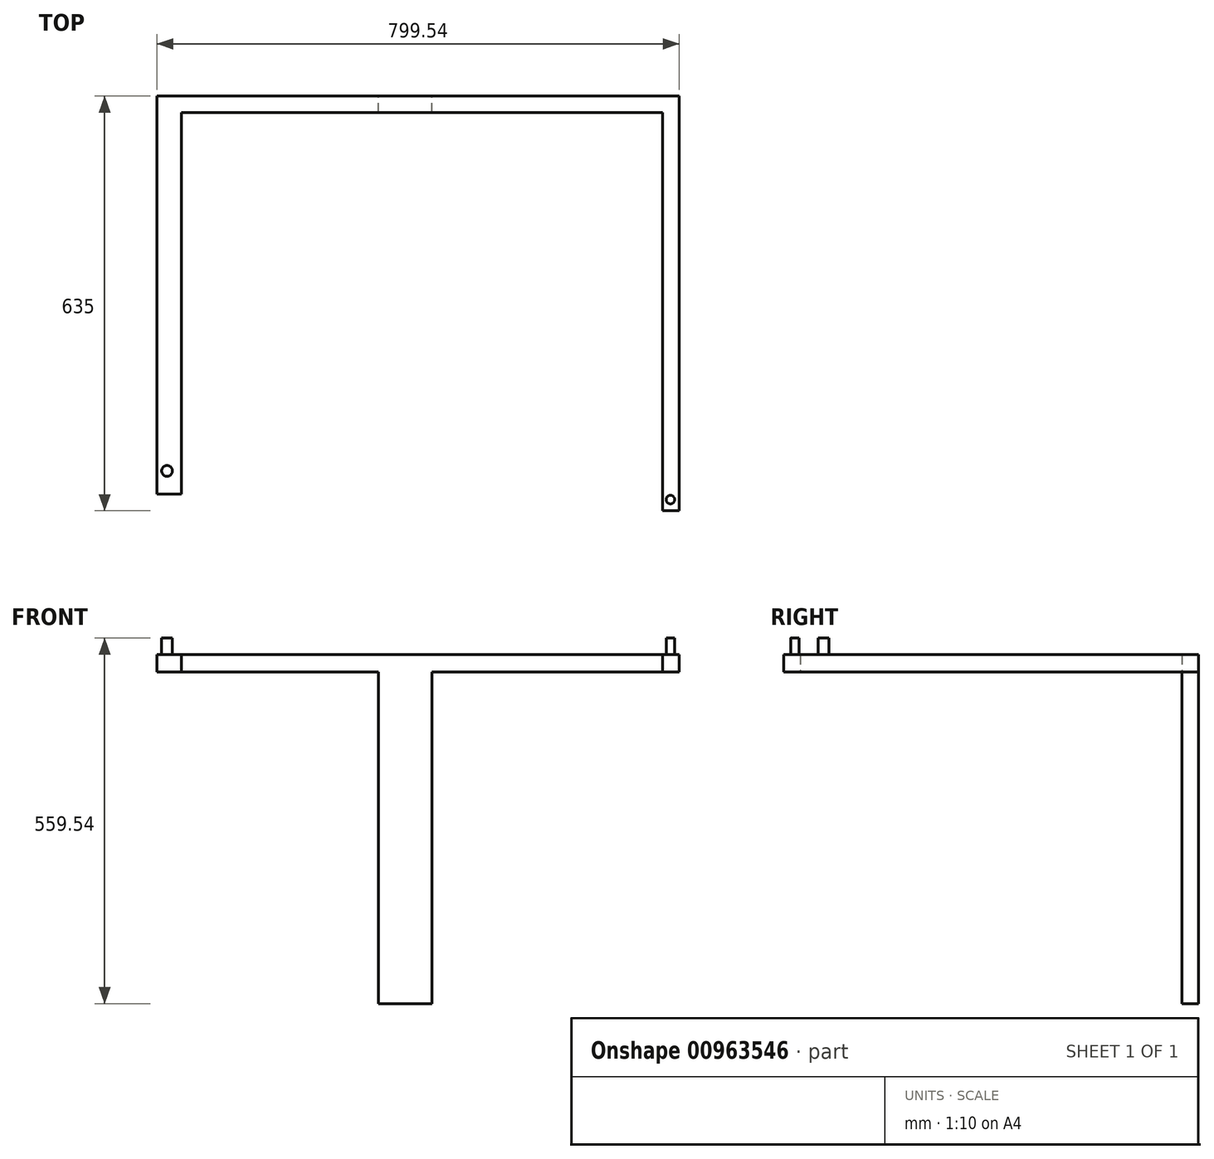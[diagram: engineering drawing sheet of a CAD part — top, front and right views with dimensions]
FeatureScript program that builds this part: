
annotation { "Feature Type Name" : "Feature", "Feature Type Description" : "" }
export const myFeature = defineFeature(function(context is Context, id is Id, definition is map)
    precondition{}
    {
        {
            var Q0;
            Q0=qCreatedBy(makeId("Front.planeOp"),FACE);
            var sketch = newSketch(context, id + "F0", { "sketchPlane" : qUnion([Q0])});
            skLineSegment(sketch, "E0.bottom", {"start": v(-18.77, 13.07) * mm, "end": v(18.77, 13.07) * mm});
            skLineSegment(sketch, "E0.top", {"start": v(-18.77, -13.07) * mm, "end": v(18.77, -13.07) * mm});
            skLineSegment(sketch, "E0.left", {"start": v(-18.77, 13.07) * mm, "end": v(-18.77, -13.07) * mm});
            skLineSegment(sketch, "E0.right", {"start": v(18.77, 13.07) * mm, "end": v(18.77, -13.07) * mm});
            skSolve(sketch);
        }
        {
            var Q0;
            Q0 = qSketchRegion(id + "F0", true);
            extrude(context, id + "F1", {"entities" : qUnion([Q0]), "oppositeDirection" : true, "depth" : 609.6 * mm, "offsetDistance" : 25.4 * mm});
        }
        {
            var Q0;
            Q0=makeQuery(id+"F1.opExtrude","SWEPT_FACE",FACE,{"disambiguationData":[OSD([sQuery(id+"F0.wireOp",EDGE,"E0.right")])]});
            var sketch = newSketch(context, id + "F2", { "sketchPlane" : qUnion([Q0])});
            skLineSegment(sketch, "E1.bottom", {"start": v(609.6, 13.07) * mm, "end": v(584.2, 13.07) * mm});
            skLineSegment(sketch, "E1.top", {"start": v(609.6, -13.07) * mm, "end": v(584.2, -13.07) * mm});
            skLineSegment(sketch, "E1.left", {"start": v(609.6, 13.07) * mm, "end": v(609.6, -13.07) * mm});
            skLineSegment(sketch, "E1.right", {"start": v(584.2, 13.07) * mm, "end": v(584.2, -13.07) * mm});
            skSolve(sketch);
        }
        {
            var Q0;
            Q0 = qSketchRegion(id + "F2", true);
            extrude(context, id + "F3", {"entities" : qUnion([Q0]), "operationType" : NewBodyOperationType.ADD, "depth" : 762 * mm, "offsetDistance" : 25.4 * mm});
        }
        {
            var Q0;
            Q0=makeQuery(id+"F3.opExtrude","SWEPT_FACE",FACE,{"disambiguationData":[OSD([sQuery(id+"F2.wireOp",EDGE,"E1.right")])]});
            var sketch = newSketch(context, id + "F4", { "sketchPlane" : qUnion([Q0])});
            skLineSegment(sketch, "E2.bottom", {"start": v(780.77, 13.07) * mm, "end": v(755.37, 13.07) * mm});
            skLineSegment(sketch, "E2.top", {"start": v(780.77, -13.07) * mm, "end": v(755.37, -13.07) * mm});
            skLineSegment(sketch, "E2.left", {"start": v(780.77, 13.07) * mm, "end": v(780.77, -13.07) * mm});
            skLineSegment(sketch, "E2.right", {"start": v(755.37, 13.07) * mm, "end": v(755.37, -13.07) * mm});
            skSolve(sketch);
        }
        {
            var Q0;
            Q0 = qSketchRegion(id + "F4", true);
            extrude(context, id + "F5", {"entities" : qUnion([Q0]), "operationType" : NewBodyOperationType.ADD, "depth" : 609.6 * mm, "offsetDistance" : 25.4 * mm});
        }
        {
            var Q0;
            Q0=makeQuery(id+"F5.boolean.opBoolean","MERGE",FACE,{"derivedFrom":[makeQuery(id+"F3.boolean.opBoolean","MERGE",FACE,{"derivedFrom":[makeQuery(id+"F1.opExtrude","SWEPT_FACE",FACE,{"disambiguationData":[OSD([sQuery(id+"F0.wireOp",EDGE,"E0.top")])]}),makeQuery(id+"F3.opExtrude","SWEPT_FACE",FACE,{"disambiguationData":[OSD([sQuery(id+"F2.wireOp",EDGE,"E1.top")])]})]}),makeQuery(id+"F5.opExtrude","SWEPT_FACE",FACE,{"disambiguationData":[OSD([sQuery(id+"F4.wireOp",EDGE,"E2.top")])]})]});
            var sketch = newSketch(context, id + "F6", { "sketchPlane" : qUnion([Q0])});
            skLineSegment(sketch, "E3.bottom", {"start": v(320.37, -584.2) * mm, "end": v(402.45, -584.2) * mm});
            skLineSegment(sketch, "E3.top", {"start": v(320.37, -609.6) * mm, "end": v(402.45, -609.6) * mm});
            skLineSegment(sketch, "E3.left", {"start": v(320.37, -584.2) * mm, "end": v(320.37, -609.6) * mm});
            skLineSegment(sketch, "E3.right", {"start": v(402.45, -584.2) * mm, "end": v(402.45, -609.6) * mm});
            skSolve(sketch);
        }
        {
            var Q0;
            Q0 = qSketchRegion(id + "F6", true);
            extrude(context, id + "F7", {"entities" : qUnion([Q0]), "operationType" : NewBodyOperationType.ADD, "depth" : 508 * mm, "offsetDistance" : 25.4 * mm});
        }
        {
            var Q0;
            Q0=makeQuery(id+"F5.boolean.opBoolean","MERGE",FACE,{"derivedFrom":[makeQuery(id+"F3.boolean.opBoolean","MERGE",FACE,{"derivedFrom":[makeQuery(id+"F1.opExtrude","SWEPT_FACE",FACE,{"disambiguationData":[OSD([sQuery(id+"F0.wireOp",EDGE,"E0.bottom")])]}),makeQuery(id+"F3.opExtrude","SWEPT_FACE",FACE,{"disambiguationData":[OSD([sQuery(id+"F2.wireOp",EDGE,"E1.bottom")])]})]}),makeQuery(id+"F5.opExtrude","SWEPT_FACE",FACE,{"disambiguationData":[OSD([sQuery(id+"F4.wireOp",EDGE,"E2.bottom")])]})]});
            var sketch = newSketch(context, id + "F8", { "sketchPlane" : qUnion([Q0])});
            skCircle(sketch, "E4", {"center": v(-3.26, 35.73) * mm, "radius": 8.3 * mm});
            skSolve(sketch);
        }
        {
            var Q0;
            Q0 = qSketchRegion(id + "F8", true);
            extrude(context, id + "F9", {"entities" : qUnion([Q0]), "operationType" : NewBodyOperationType.ADD, "depth" : 25.4 * mm, "offsetDistance" : 25.4 * mm});
        }
        {
            var Q0;
            Q0=makeQuery(id+"F5.boolean.opBoolean","MERGE",FACE,{"derivedFrom":[makeQuery(id+"F3.boolean.opBoolean","MERGE",FACE,{"derivedFrom":[makeQuery(id+"F1.opExtrude","SWEPT_FACE",FACE,{"disambiguationData":[OSD([sQuery(id+"F0.wireOp",EDGE,"E0.bottom")])]}),makeQuery(id+"F3.opExtrude","SWEPT_FACE",FACE,{"disambiguationData":[OSD([sQuery(id+"F2.wireOp",EDGE,"E1.bottom")])]})]}),makeQuery(id+"F5.opExtrude","SWEPT_FACE",FACE,{"disambiguationData":[OSD([sQuery(id+"F4.wireOp",EDGE,"E2.bottom")])]})]});
            var sketch = newSketch(context, id + "F10", { "sketchPlane" : qUnion([Q0])});
            skCircle(sketch, "E5", {"center": v(767.28, -8.23) * mm, "radius": 6.53 * mm});
            skSolve(sketch);
        }
        {
            var Q0;
            Q0 = qSketchRegion(id + "F10", true);
            extrude(context, id + "F11", {"entities" : qUnion([Q0]), "operationType" : NewBodyOperationType.ADD, "depth" : 25.4 * mm, "offsetDistance" : 25.4 * mm});
        }
    });
